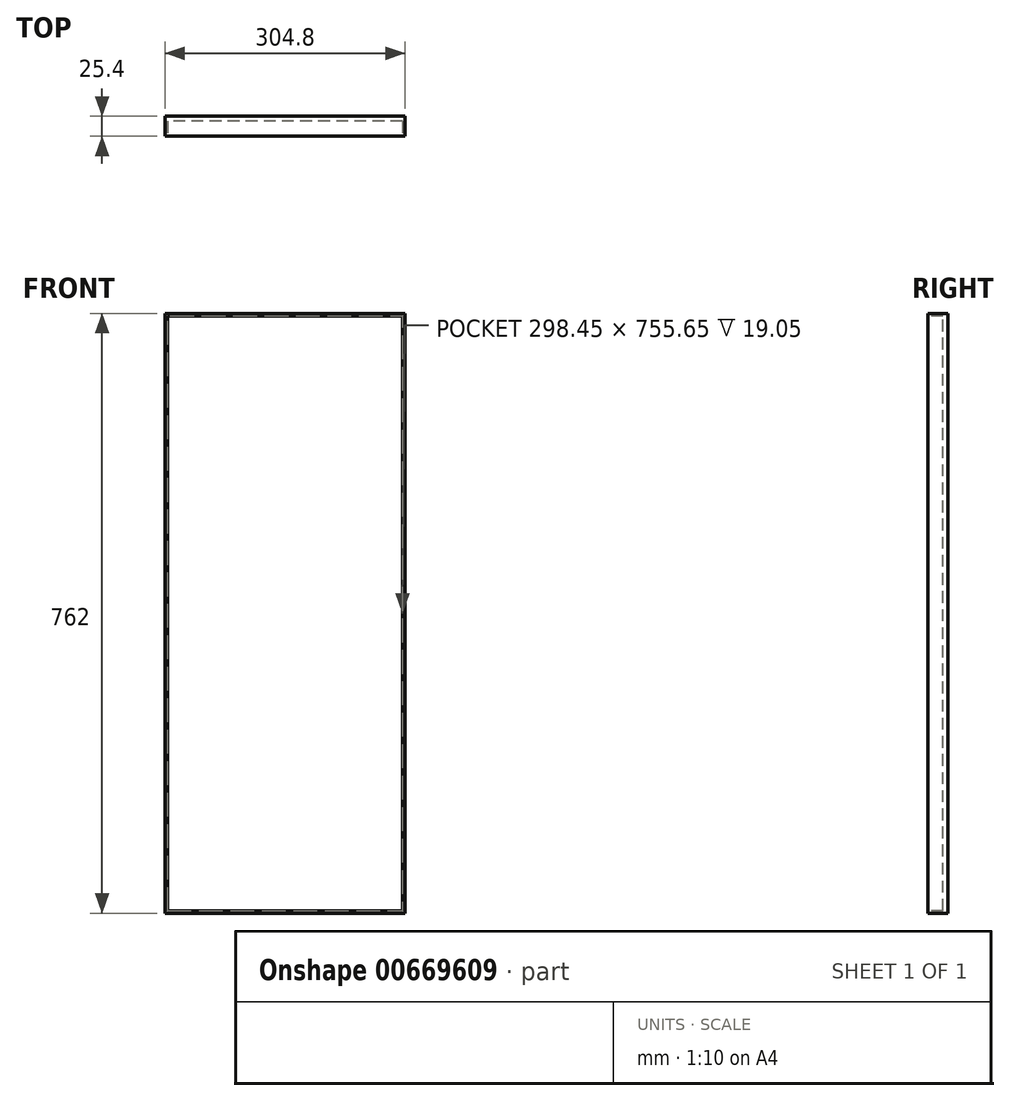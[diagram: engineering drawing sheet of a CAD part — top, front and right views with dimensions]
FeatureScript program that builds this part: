
annotation { "Feature Type Name" : "Feature", "Feature Type Description" : "" }
export const myFeature = defineFeature(function(context is Context, id is Id, definition is map)
    precondition{}
    {
        {
            var Q0;
            Q0=qCreatedBy(makeId("Front.planeOp"),FACE);
            var sketch = newSketch(context, id + "F0", { "sketchPlane" : qUnion([Q0])});
            skLineSegment(sketch, "E0.bottom", {"start": v(0, 0) * mm, "end": v(304.8, 0) * mm});
            skLineSegment(sketch, "E0.top", {"start": v(0, 762) * mm, "end": v(304.8, 762) * mm});
            skLineSegment(sketch, "E0.left", {"start": v(0, 0) * mm, "end": v(0, 762) * mm});
            skLineSegment(sketch, "E0.right", {"start": v(304.8, 0) * mm, "end": v(304.8, 762) * mm});
            skSolve(sketch);
        }
        {
            var Q0;
            Q0 = qSketchRegion(id + "F0", true);
            extrude(context, id + "F1", {"entities" : qUnion([Q0]), "depth" : 25.4 * mm, "offsetDistance" : 25.4 * mm});
        }
        {
            var Q0;
            Q0=makeQuery(id+"F1.opExtrude","CAP_FACE",FACE,{"disambiguationData":[OSD([sQuery(id+"F0.wireOp",EDGE,"E0.bottom"),sQuery(id+"F0.wireOp",EDGE,"E0.top"),sQuery(id+"F0.wireOp",EDGE,"E0.left"),sQuery(id+"F0.wireOp",EDGE,"E0.right")])],"isStart":false});
            var sketch = newSketch(context, id + "F2", { "sketchPlane" : qUnion([Q0])});
            skLineSegment(sketch, "E1.bottom", {"start": v(301.62, 3.18) * mm, "end": v(3.18, 3.17) * mm});
            skLineSegment(sketch, "E1.top", {"start": v(301.62, 758.83) * mm, "end": v(3.17, 758.83) * mm});
            skLineSegment(sketch, "E1.left", {"start": v(301.62, 3.18) * mm, "end": v(301.62, 758.83) * mm});
            skLineSegment(sketch, "E1.right", {"start": v(3.18, 3.17) * mm, "end": v(3.17, 758.83) * mm});
            skSolve(sketch);
        }
        {
            var Q0;
            Q0 = qSketchRegion(id + "F2", true);
            var Q1;
            Q1=makeQuery(id+"F2.imprint","IMPRINT",FACE,{"disambiguationData":[TD([[makeQuery(id+"F2.imprint","IMPRINT",EDGE,{"derivedFrom":sQuery(id+"F2.wireOp",EDGE,"E1.bottom")}),-1.0]])]});
            extrude(context, id + "F3", {"entities" : qUnion([Q0, Q1]), "operationType" : NewBodyOperationType.REMOVE, "oppositeDirection" : true, "depth" : 19.05 * mm, "offsetDistance" : 25.4 * mm});
        }
    });
